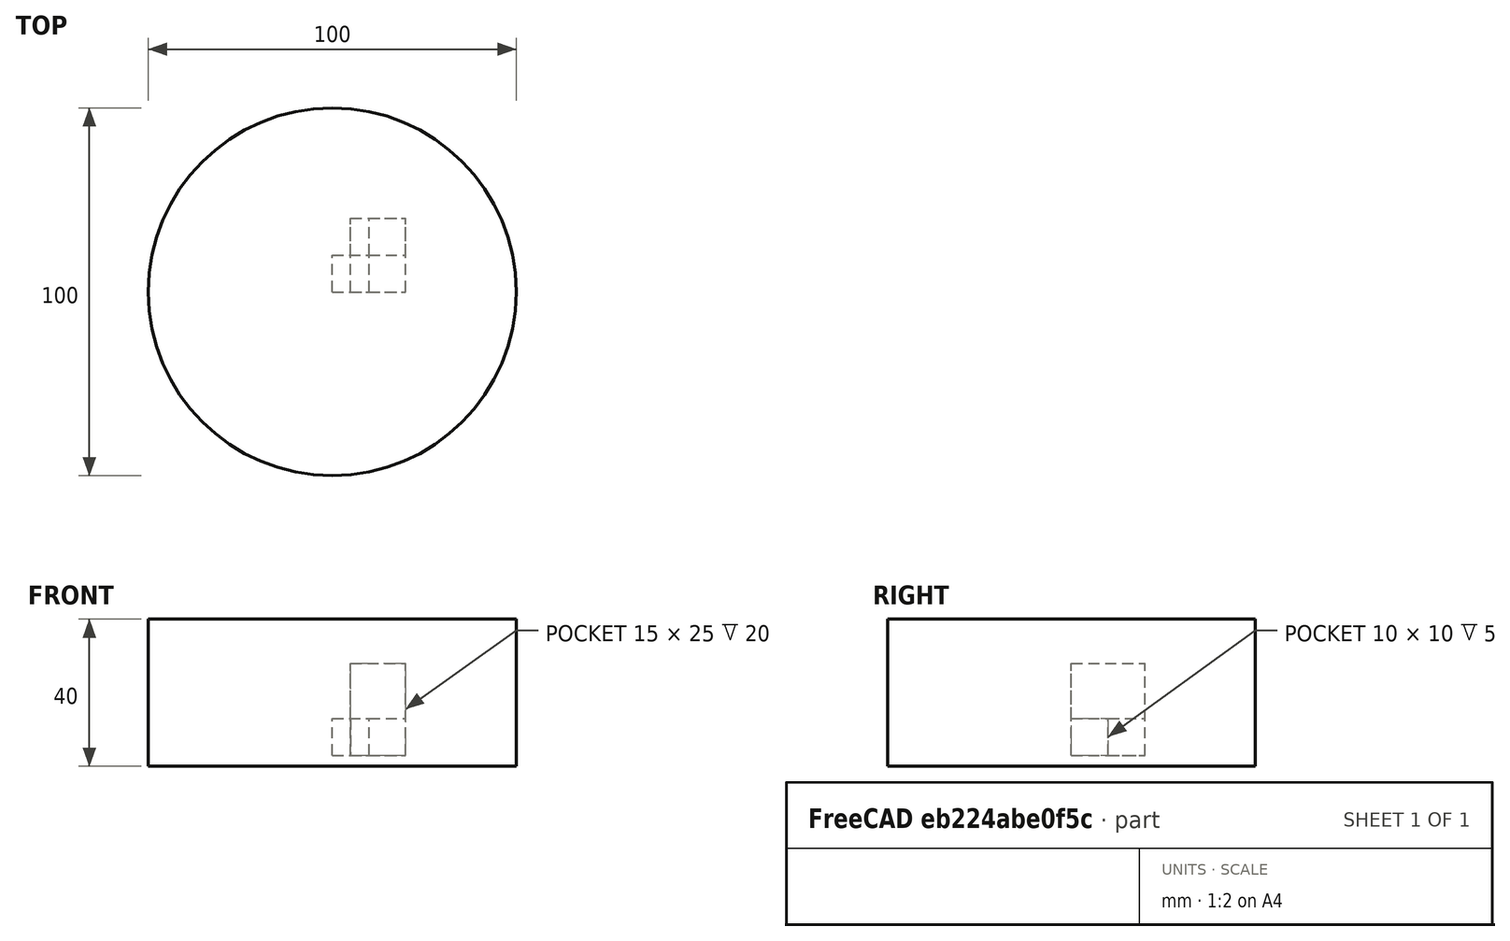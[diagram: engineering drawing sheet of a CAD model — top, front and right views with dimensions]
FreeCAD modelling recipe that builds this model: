
FCSTD DOCUMENT  (FreeCAD 0.17R13528 (Git))
Label: test-objects
License: All rights reserved
LicenseURL: http://en.wikipedia.org/wiki/All_rights_reserved
objects: Part::Box×4, Part::MultiFuse×2, Part::Cylinder×1, Part::Cut×1
note: 8 computed .brp shape members not serialized (recipe doc carries the construction recipe); baked Part::Feature solids carry a one-line shape summary decoded from their .brp

FEATURE [Part::Box] Box  label="Cube"
  AttacherType = Attacher::AttachEngine3D
  Height = 10
  Length = 10
  Width = 10
FEATURE [Part::Box] Box001  label="Cube001"
  AttacherType = Attacher::AttachEngine3D
  Height = 25
  Length = 15
  Placement = pos=(5,0,0) rot=(0,0,1;0rad)
  Width = 20
FEATURE [Part::MultiFuse] Fusion
  Shapes = -> [Box,Box001]
FEATURE [Part::Cylinder] Cylinder
  Angle = 360
  AttacherType = Attacher::AttachEngine3D
  Height = 40
  Placement = pos=(0,0,-3) rot=(0,0,1;0rad)
  Radius = 50
FEATURE [Part::Cut] Cut
  Base = -> Cylinder
  Tool = -> Fusion
FEATURE [Part::Box] Box002  label="Cube002"
  AttacherType = Attacher::AttachEngine3D
  Height = 10
  Length = 10
  Width = 10
FEATURE [Part::Box] Box003  label="Cube003"
  AttacherType = Attacher::AttachEngine3D
  Height = 10
  Length = 10
  Placement = pos=(10,10,0) rot=(0,0,1;0rad)
  Width = 10
FEATURE [Part::MultiFuse] Fusion001
  Shapes = -> [Box002,Box003]
